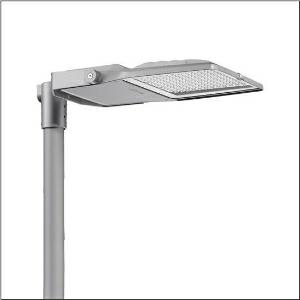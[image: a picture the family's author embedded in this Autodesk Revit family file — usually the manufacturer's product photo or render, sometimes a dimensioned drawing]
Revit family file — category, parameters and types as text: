
# Revit family: floodlight_fl_21_midi___pl52_5xa7786f4d3a_c4a6
name_source: partatom
category: Lighting Fixtures
units: mm (PartAtom-declared; Revit-internal decimal feet)

## family parameters
Cut with Voids When Loaded = No
Host = Face
Light Source = No
Part Type = Normal
Room Calculation Point = No
Round Connector Dimension = Use Diameter
Shared = No

## types (1)
- --- (1 x LED, 37330 lm, 271.6 W, 4000K)
    Apparent Load = 272 VA
    CIE Flux Codes = 26 60 98 100 100
    Color Rendering = 70
    Color Temperature = 4000K
    Default Elevation = 1800 mm
    Description = Floodlight FL 21 midi, floodlight, primary light control with lens, of PMMA, primary optical cover: protective disc, of toughened safety glass, transparent, light distribution: PL52, light emission: direct distribution, installation type: surface-mounted, LED, High Power LED, rated luminous flux: 37.330lm, luminous efficacy: 137lm/W, light colour: 740, colour temperature: 4000K, control gear: Smart Interface (Zhaga)D4i, control: overheat protection, constant luminous flux control, time-dependent luminous flux control, flexible luminous flux parameterisation, pre-setting: logarithmic dimming characteristic, with terminal, 6-pole, mains connection: 220..240V, AC, 50/60Hz, start of lifetime: 272W, end of service life: 287W, reduction: 123W, mast bracket, of diecast aluminium, powder-coated, Siteco® metallic grey (DB 702S), corrosivity category C5 mid according to DIN EN ISO 12944, suitable for swimming pools, chlorine-resistant, sealing non-destructively replaceable, mast bracket, of steel, galvanised, powder-coated, Siteco® metallic grey (DB 702S), Smart Interface below and above, protection rating (complete): IP66, insulation class (complete): insulation class II (safety insulation), certification: CE, ENEC, VDE, protection symbol: D, impact resistance: IK08, permissible operating ambient temperature: -40..+40°C, permissible operating ambient temperature for outdoor applications: -40..+50°C, standard: DIN EN 12944, LABS conformity tested according to VDMA 24364:2018-05, packaging unit: 1 piece

Light Distribution: PL52
    Height = 76 mm
    Lamp = 1 x LED
    Lamp Light Flux = 37330 lm
    Lamp Power = 271.6 W
    Lamp count = 1
    Length = 657 mm
    Luminous efficacy = 137 lm/W
    Manufacturer = Siteco
    ModVariant = No
    Model = 5XA7786F4D3A
    Number of Poles = 1
    OnlyDefault = Yes
    Power Factor = 1
    Product Name = Floodlight FL 21 midi | PL52
    Product group = floodlight | pylon annexe
    ProductGroupID = 6200
    Protection Class = Protection class II
    Protection Degree = IP 66
    RLX_Detail_Level = 1
    RLX_Emergency_Light_Flux = 0 lm
    RLX_Emergency_Type = 0
    RLX_Emergency_Type_DB = No
    RlxData = <blob elided: 104897 chars, md5=85483f2b>
    Socket = socket
    Standby Power = 0 W
    System Light Flux = 37330 lm
    System Power = 272 W
    Type Comments = factory setting: luminous flux: 100 % | dim-lin: 254 | 620 mA
    Type Image = l_1007123.jpg
    URL = http://relux.com
    VarID = @adj_089256
    Voltage = 0 V
    Weight = 0.00 kg
    Width = 442 mm

## geometry (parser evidence)
native form markers: Blend x4, Sweep x11
no freeform markers — native parametric forms only
